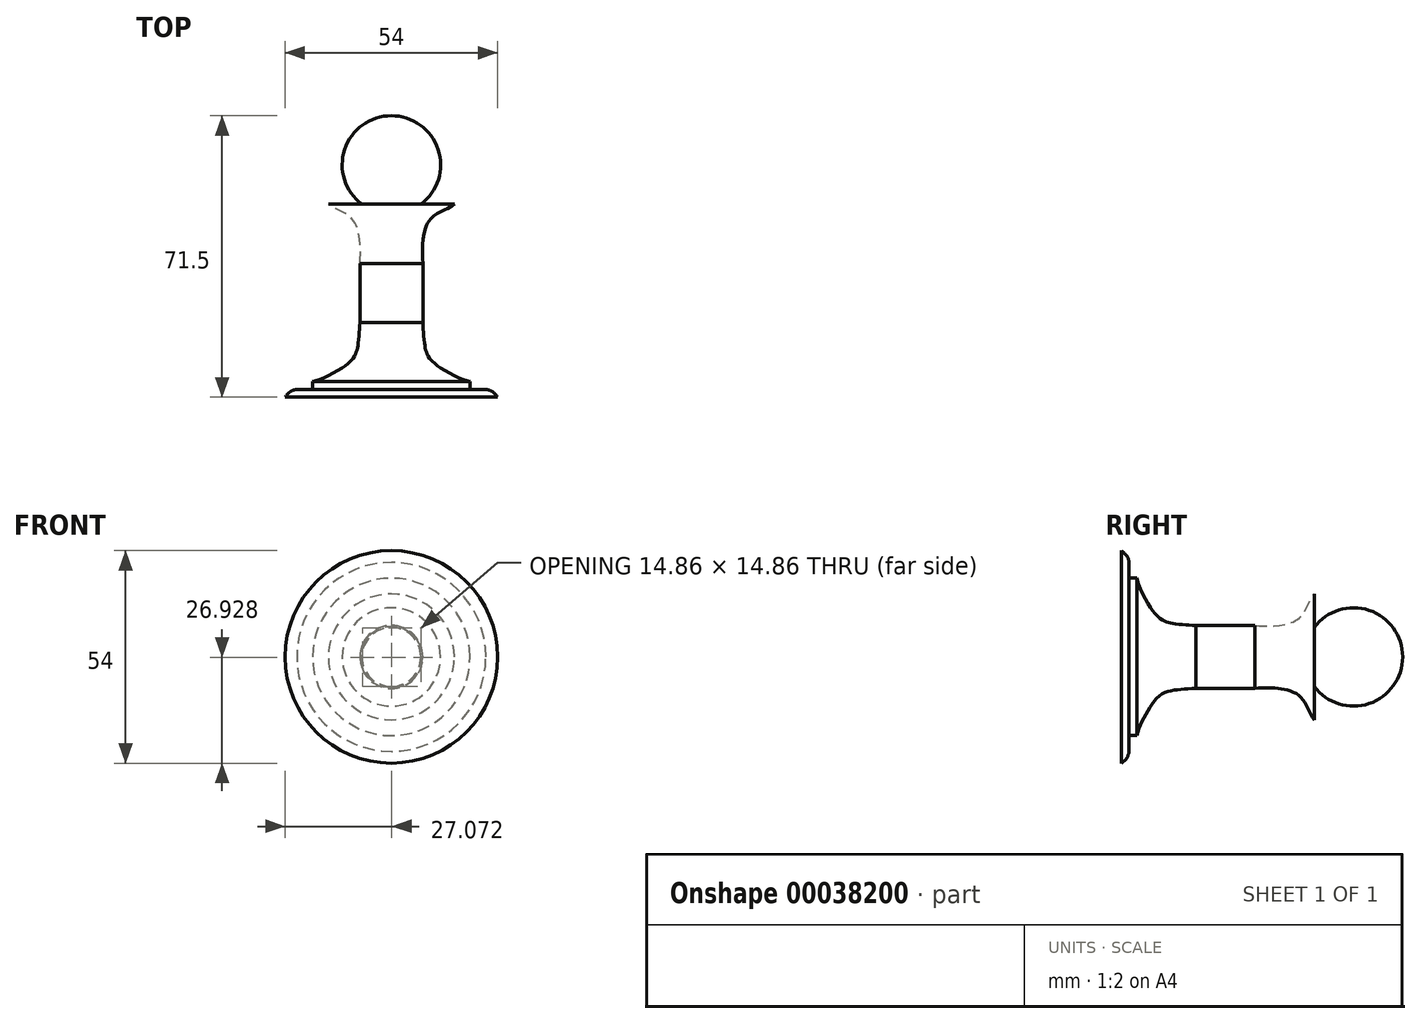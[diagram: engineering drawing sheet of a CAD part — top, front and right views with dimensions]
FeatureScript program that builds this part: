
annotation { "Feature Type Name" : "Feature", "Feature Type Description" : "" }
export const myFeature = defineFeature(function(context is Context, id is Id, definition is map)
    precondition{}
    {
        {
            var Q0;
            Q0=qCreatedBy(makeId("Top.planeOp"),FACE);
            var sketch = newSketch(context, id + "F0", { "sketchPlane" : qUnion([Q0])});
            skArc(sketch, "E0", {"start": v(7.5, 25.64) * mm, "mid": v(11.86, 39.6) * mm, "end": v(0, 48.14) * mm});
            skLineSegment(sketch, "E1", {"start": v(0, 35.64) * mm, "end": v(0, 25.64) * mm});
            skLineSegment(sketch, "E2", {"start": v(0, 25.64) * mm, "end": v(0, 10.64) * mm});
            skLineSegment(sketch, "E3", {"start": v(7.5, 25.64) * mm, "end": v(16, 25.64) * mm});
            skLineSegment(sketch, "E4", {"start": v(8, 10.64) * mm, "end": v(8, -4.36) * mm});
            skLineSegment(sketch, "E5", {"start": v(0, -4.36) * mm, "end": v(0, -19.36) * mm});
            skLineSegment(sketch, "E6", {"start": v(0, -19.36) * mm, "end": v(0, -21.36) * mm});
            skLineSegment(sketch, "E7", {"start": v(0, -21.36) * mm, "end": v(0, -23.36) * mm});
            skLineSegment(sketch, "E8", {"start": v(0, -23.36) * mm, "end": v(27, -23.36) * mm});
            skLineSegment(sketch, "E9", {"start": v(20, -21.36) * mm, "end": v(24, -21.36) * mm});
            skLineSegment(sketch, "E10", {"start": v(0, 35.64) * mm, "end": v(0, 48.14) * mm});
            skLineSegment(sketch, "E11", {"start": v(0, 10.64) * mm, "end": v(0, -4.36) * mm});
            skFitSpline(sketch, "E12", {"points": [v(16, 25.64) * mm, v(10.42, 22.42) * mm, v(8.08, 17.09) * mm, v(8, 10.64) * mm], "startDerivative": vector(-14.09, -11.06) * mm, "endDerivative": vector(1.46, -20.17) * mm});
            skFitSpline(sketch, "E13", {"points": [v(8, -4.36) * mm, v(8.42, -9.75) * mm, v(9.9, -13.69) * mm, v(14.57, -17.11) * mm, v(20, -19.36) * mm], "startDerivative": vector(1.33, -24.48) * mm, "endDerivative": vector(21.36, -4.3) * mm});
            skLineSegment(sketch, "E14", {"start": v(20, -19.36) * mm, "end": v(20, -21.36) * mm});
            skFitSpline(sketch, "E15", {"points": [v(24, -21.36) * mm, v(25.65, -21.95) * mm, v(27, -23.36) * mm], "startDerivative": vector(3.82, -1.01) * mm, "endDerivative": vector(2.16, -3) * mm});
            skSolve(sketch);
        }
        {
            var Q0;
            Q0=makeQuery(id+"F0.imprint","IMPRINT",FACE,{"disambiguationData":[TD([[makeQuery(id+"F0.imprint","IMPRINT",EDGE,{"derivedFrom":sQuery(id+"F0.wireOp",EDGE,"E0")}),1.0]])]});
            var Q1;
            Q1=sQuery(id+"F0.wireOp",EDGE,"E10");
            revolve(context, id + "F1", {"entities" : qUnion([Q0]), "axis" : qUnion([Q1]), "revolveType" : RevolveType.FULL});
        }
    });
